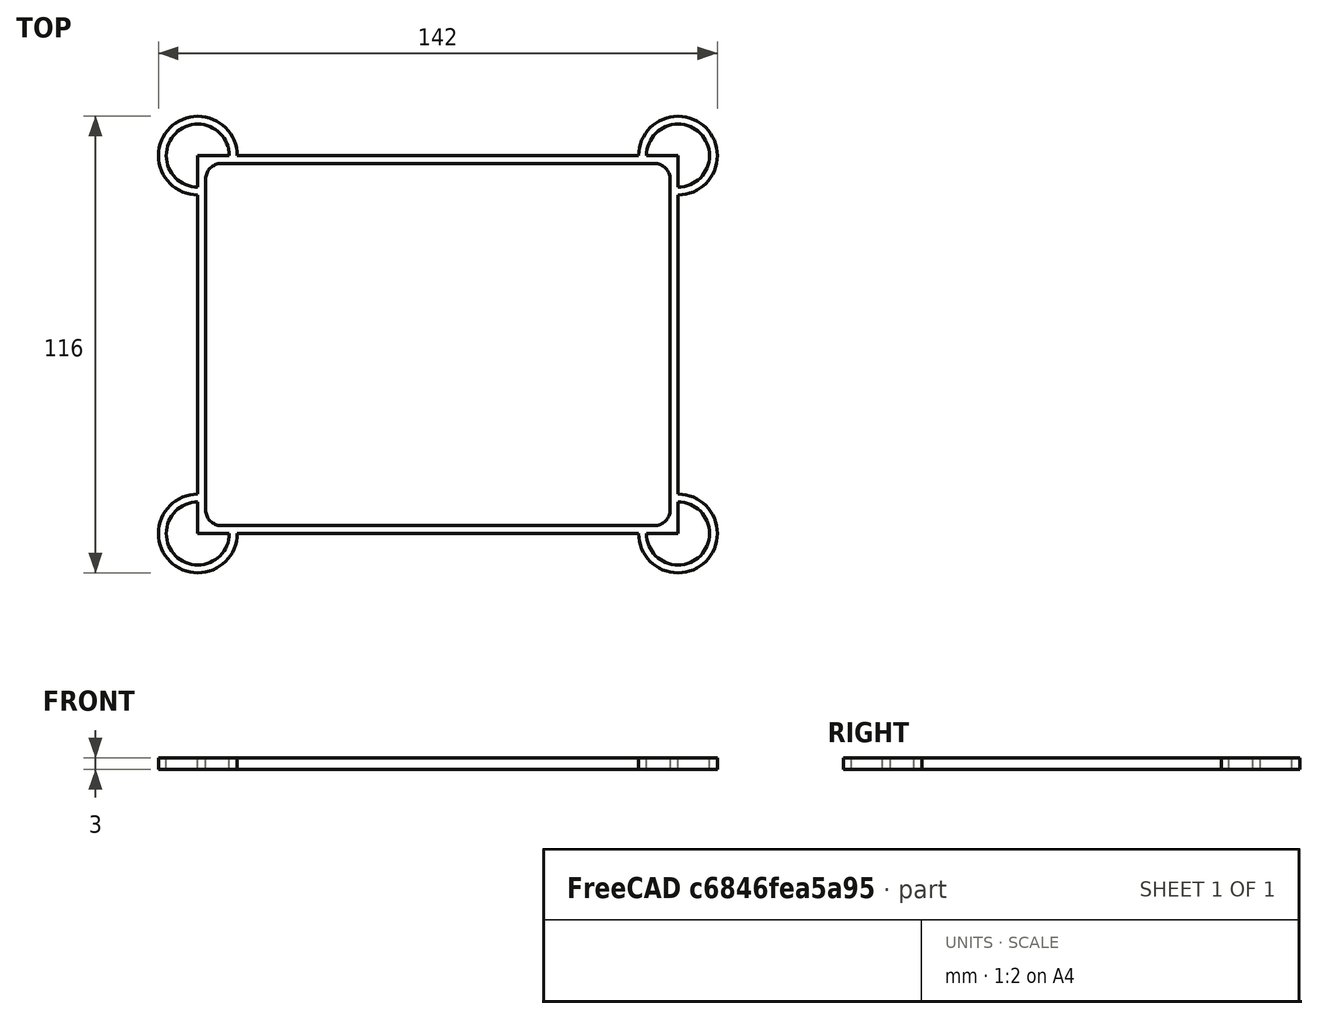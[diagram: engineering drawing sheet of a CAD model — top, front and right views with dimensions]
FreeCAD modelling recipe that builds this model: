
FCSTD DOCUMENT  (FreeCAD 0.18.4R)
Label: PrintFrameBox
License: All rights reserved
LicenseURL: http://en.wikipedia.org/wiki/All_rights_reserved
objects: Part::Box×8, Part::Cylinder×8, Part::MultiFuse×6, Part::Cut×4, Part::Fillet×1, Mesh::Feature×1
note: 27 computed .brp shape members not serialized (recipe doc carries the construction recipe); baked Part::Feature solids carry a one-line shape summary decoded from their .brp

FEATURE [Part::Box] Box  label="Würfel001"
  AttacherType = Attacher::AttachEngine3D
  Height = 3
  Length = 120
  Width = 2
FEATURE [Part::Box] Box001  label="Würfel002"
  AttacherType = Attacher::AttachEngine3D
  Height = 3
  Length = 120
  Placement = pos=(0,94,0) rot=(0,0,1;0rad)
  Width = 2
FEATURE [Part::Box] Box002  label="Würfel003"
  AttacherType = Attacher::AttachEngine3D
  Height = 3
  Length = 2
  Placement = pos=(-2,0,0) rot=(0,0,1;0rad)
  Width = 96
FEATURE [Part::Box] Box003  label="Würfel004"
  AttacherType = Attacher::AttachEngine3D
  Height = 3
  Length = 2
  Placement = pos=(118,0,0) rot=(0,0,1;0rad)
  Width = 96
FEATURE [Part::MultiFuse] Fusion  label="Rahmen"
  Shapes = -> [Box,Box002,Box001,Box003]
FEATURE [Part::Cylinder] Cylinder  label="Zylinder002"
  Angle = 360
  AttacherType = Attacher::AttachEngine3D
  Height = 5
  Placement = pos=(-2,0,-1) rot=(0,0,1;0rad)
  Radius = 8
FEATURE [Part::Cylinder] Cylinder001  label="Zylinder001"
  Angle = 360
  AttacherType = Attacher::AttachEngine3D
  Height = 3
  Placement = pos=(-2,0,0) rot=(0,0,1;0rad)
  Radius = 10
FEATURE [Part::Box] Box004  label="Würfel"
  AttacherType = Attacher::AttachEngine3D
  Height = 5
  Length = 10
  Placement = pos=(-2,0,-1) rot=(0,0,1;0rad)
  Width = 10
FEATURE [Part::MultiFuse] Fusion001
  Shapes = -> [Cylinder,Box004]
FEATURE [Part::Cut] Cut  label="Ecke001"
  Base = -> Cylinder001
  Tool = -> Fusion001
FEATURE [Part::Cylinder] Cylinder002  label="Zylinder003"
  Angle = 360
  AttacherType = Attacher::AttachEngine3D
  Height = 3
  Placement = pos=(-2,0,0) rot=(0,0,1;0rad)
  Radius = 10
FEATURE [Part::Box] Box005  label="Würfel005"
  AttacherType = Attacher::AttachEngine3D
  Height = 5
  Length = 10
  Placement = pos=(-2,0,-1) rot=(0,0,1;0rad)
  Width = 10
FEATURE [Part::Cylinder] Cylinder003  label="Zylinder004"
  Angle = 360
  AttacherType = Attacher::AttachEngine3D
  Height = 5
  Placement = pos=(-2,0,-1) rot=(0,0,1;0rad)
  Radius = 8
FEATURE [Part::MultiFuse] Fusion002
  Shapes = -> [Cylinder003,Box005]
FEATURE [Part::Cut] Cut001  label="Ecke002"
  Base = -> Cylinder002
  Placement = pos=(-2,94,0) rot=(0,0,-1;1.5708rad)
  Tool = -> Fusion002
FEATURE [Part::Cylinder] Cylinder004  label="Zylinder005"
  Angle = 360
  AttacherType = Attacher::AttachEngine3D
  Height = 3
  Placement = pos=(-2,0,0) rot=(0,0,1;0rad)
  Radius = 10
FEATURE [Part::Box] Box006  label="Würfel006"
  AttacherType = Attacher::AttachEngine3D
  Height = 5
  Length = 10
  Placement = pos=(-2,0,-1) rot=(0,0,1;0rad)
  Width = 10
FEATURE [Part::Cylinder] Cylinder005  label="Zylinder006"
  Angle = 360
  AttacherType = Attacher::AttachEngine3D
  Height = 5
  Placement = pos=(-2,0,-1) rot=(0,0,1;0rad)
  Radius = 8
FEATURE [Part::MultiFuse] Fusion003
  Shapes = -> [Cylinder005,Box006]
FEATURE [Part::Cut] Cut002  label="Ecke003"
  Base = -> Cylinder004
  Placement = pos=(120,2,0) rot=(0,0,1;1.5708rad)
  Tool = -> Fusion003
FEATURE [Part::Cylinder] Cylinder006  label="Zylinder007"
  Angle = 360
  AttacherType = Attacher::AttachEngine3D
  Height = 3
  Placement = pos=(-2,0,0) rot=(0,0,1;0rad)
  Radius = 10
FEATURE [Part::Box] Box007  label="Würfel007"
  AttacherType = Attacher::AttachEngine3D
  Height = 5
  Length = 10
  Placement = pos=(-2,0,-1) rot=(0,0,1;0rad)
  Width = 10
FEATURE [Part::Cylinder] Cylinder007  label="Zylinder008"
  Angle = 360
  AttacherType = Attacher::AttachEngine3D
  Height = 5
  Placement = pos=(-2,0,-1) rot=(0,0,1;0rad)
  Radius = 8
FEATURE [Part::MultiFuse] Fusion004
  Shapes = -> [Cylinder007,Box007]
FEATURE [Part::Cut] Cut003  label="Ecke004"
  Base = -> Cylinder006
  Placement = pos=(118,96,0) rot=(0,0,1;3.14159rad)
  Tool = -> Fusion004
FEATURE [Part::MultiFuse] Fusion005
  Shapes = -> [Cut003,Fusion,Cut002,Cut,Cut001]
FEATURE [Part::Fillet] Fillet
  Base = -> Fusion005
  Edges = 4 edges r=4: [Edge33,Edge34,Edge69,Edge77]
FEATURE [Mesh::Feature] Mesh  label="Fillet (Meshed)"
